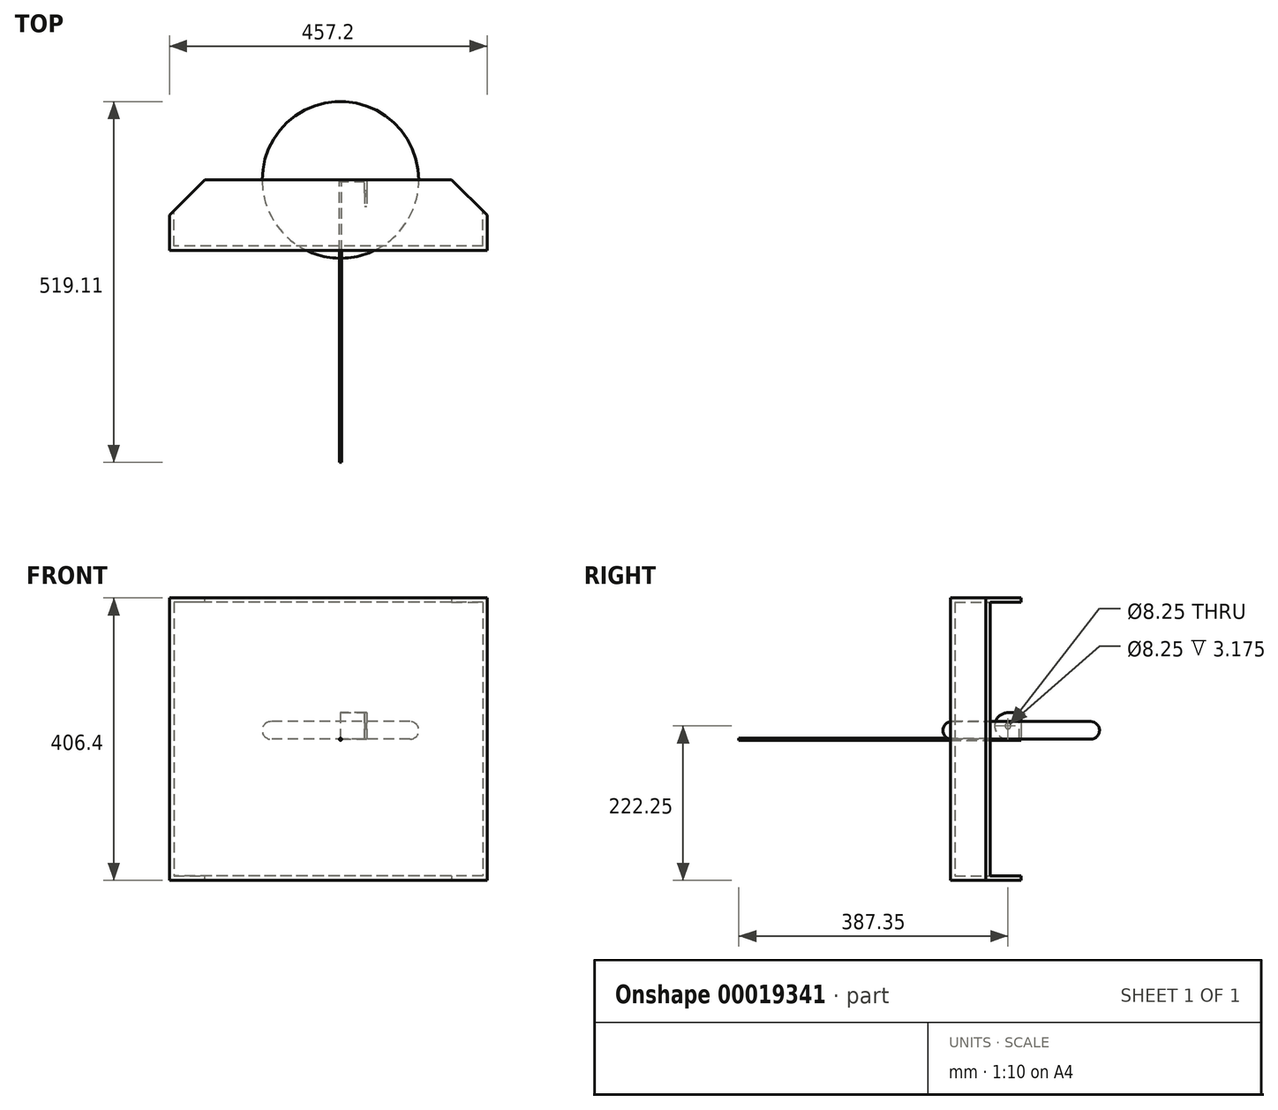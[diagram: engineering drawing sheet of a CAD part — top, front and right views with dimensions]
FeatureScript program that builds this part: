
annotation { "Feature Type Name" : "Feature", "Feature Type Description" : "" }
export const myFeature = defineFeature(function(context is Context, id is Id, definition is map)
    precondition{}
    {
        {
            var Q0;
            Q0=qCreatedBy(makeId("Top.planeOp"),FACE);
            var sketch = newSketch(context, id + "F0", { "sketchPlane" : qUnion([Q0])});
            skCircle(sketch, "E0", {"center": v(0, 0) * mm, "radius": 112.71 * mm});
            skSolve(sketch);
        }
        {
            var Q0;
            Q0=qSketchRegion(id+"F0",true);
            extrude(context, id + "F1", {"entities" : qUnion([Q0]), "depth" : 25.4 * mm});
        }
        {
            var Q0;
            Q0=qCreatedBy(makeId("Front.planeOp"),FACE);
            var sketch = newSketch(context, id + "F2", { "sketchPlane" : qUnion([Q0])});
            skCircle(sketch, "E1", {"center": v(0, 0) * mm, "radius": 1.59 * mm});
            skSolve(sketch);
        }
        {
            var Q0;
            Q0=qSketchRegion(id+"F2",true);
            extrude(context, id + "F3", {"entities" : qUnion([Q0]), "depth" : 406.4 * mm});
        }
        {
            var Q0;
            Q0=makeQuery(id+"F1.opExtrude","CAP_EDGE",EDGE,{"disambiguationData":[OSD([sQuery(id+"F0.wireOp",EDGE,"E0")])],"isStart":false});
            var Q1;
            Q1=makeQuery(id+"F1.opExtrude","CAP_EDGE",EDGE,{"disambiguationData":[OSD([sQuery(id+"F0.wireOp",EDGE,"E0")])],"isStart":true});
            fillet(context, id + "F4", {"entities" : qUnion([Q0, Q1]), "radius" : 12.7 * mm, "tangentPropagation" : true, "allowEdgeOverflow" : false});
        }
        {
            var Q0;
            Q0=qCreatedBy(makeId("Front.planeOp"),FACE);
            var sketch = newSketch(context, id + "F5", { "sketchPlane" : qUnion([Q0])});
            skLineSegment(sketch, "E2.rect.bottom", {"start": v(210.87, 203.2) * mm, "end": v(-246.33, 203.2) * mm});
            skLineSegment(sketch, "E2.rect.top", {"start": v(210.87, -203.2) * mm, "end": v(-246.33, -203.2) * mm});
            skLineSegment(sketch, "E2.rect.left", {"start": v(210.87, 203.2) * mm, "end": v(210.87, -203.2) * mm});
            skLineSegment(sketch, "E2.rect.right", {"start": v(-246.33, 203.2) * mm, "end": v(-246.33, -203.2) * mm});
            skPoint(sketch, "E2.rect.middle", {"position": v(-17.73, 0) * mm});
            skSolve(sketch);
        }
        {
            var Q0;
            Q0=qSketchRegion(id+"F5",true);
            extrude(context, id + "F6", {"entities" : qUnion([Q0]), "depth" : 101.6 * mm});
        }
        {
            var Q0;
            Q0=makeQuery(id+"F6.opExtrude","CAP_FACE",FACE,{"disambiguationData":[OSD([sQuery(id+"F5.wireOp",EDGE,"E2.rect.bottom"),sQuery(id+"F5.wireOp",EDGE,"E2.rect.top"),sQuery(id+"F5.wireOp",EDGE,"E2.rect.left"),sQuery(id+"F5.wireOp",EDGE,"E2.rect.right")])],"isStart":true});
            shell(context, id + "F7", {"entities" : qUnion([Q0]), "thickness" : 6.35 * mm});
        }
        {
            var Q0;
            Q0=makeQuery(id+"F6.opExtrude","CAP_EDGE",EDGE,{"disambiguationData":[OSD([sQuery(id+"F5.wireOp",EDGE,"E2.rect.left")])],"isStart":true});
            var Q1;
            Q1=makeQuery(id+"F6.opExtrude","CAP_EDGE",EDGE,{"disambiguationData":[OSD([sQuery(id+"F5.wireOp",EDGE,"E2.rect.right")])],"isStart":true});
            chamfer(context, id + "F8", {"entities" : qUnion([Q0, Q1]), "width" : 50.8 * mm, "tangentPropagation" : true});
        }
        {
            var Q0;
            Q0=qCreatedBy(makeId("Top.planeOp"),FACE);
            var sketch = newSketch(context, id + "F9", { "sketchPlane" : qUnion([Q0])});
            skLineSegment(sketch, "E3", {"start": v(0, 0) * mm, "end": v(38.1, 0) * mm});
            skLineSegment(sketch, "E4", {"start": v(38.1, 0) * mm, "end": v(38.1, -38.1) * mm});
            skLineSegment(sketch, "E5", {"start": v(38.1, -38.1) * mm, "end": v(34.93, -38.1) * mm});
            skLineSegment(sketch, "E6", {"start": v(34.93, -38.1) * mm, "end": v(34.93, -3.17) * mm});
            skLineSegment(sketch, "E7", {"start": v(34.92, -3.18) * mm, "end": v(0, -3.18) * mm});
            skLineSegment(sketch, "E8", {"start": v(0, -3.17) * mm, "end": v(0, 0) * mm});
            skSolve(sketch);
        }
        {
            var Q0;
            Q0=qSketchRegion(id+"F9",true);
            extrude(context, id + "F10", {"entities" : qUnion([Q0]), "depth" : 38.1 * mm});
        }
        {
            var Q0;
            Q0=makeQuery(id+"F10.opExtrude","SWEPT_FACE",FACE,{"disambiguationData":[OSD([sQuery(id+"F9.wireOp",EDGE,"E4")])]});
            var sketch = newSketch(context, id + "F11", { "sketchPlane" : qUnion([Q0])});
            skLineSegment(sketch, "E9", {"start": v(-19.05, 0) * mm, "end": v(-19.05, 38.1) * mm, "construction": true});
            skCircle(sketch, "E10", {"center": v(-19.05, 19.05) * mm, "radius": 4.12 * mm});
            skSolve(sketch);
        }
        {
            var Q0;
            Q0=makeQuery(id+"F11.imprint","IMPRINT",FACE,{"disambiguationData":[TD([[makeQuery(id+"F11.imprint","IMPRINT",EDGE,{"derivedFrom":sQuery(id+"F11.wireOp",EDGE,"E10")}),1.0]])]});
            var Q1;
            Q1=sQuery(id+"F11.wireOp",EDGE,"E10");
            extrude(context, id + "F12", {"entities" : qUnion([Q0]), "operationType" : NewBodyOperationType.REMOVE, "surfaceEntities" : qUnion([Q1]), "endBound" : BoundingType.UP_TO_NEXT, "oppositeDirection" : true, "depth" : 25.4 * mm});
        }
        {
            var Q0;
            Q0=makeQuery(id+"F10.opExtrude","CAP_EDGE",EDGE,{"disambiguationData":[OSD([sQuery(id+"F9.wireOp",EDGE,"E5")])],"isStart":true});
            var Q1;
            Q1=makeQuery(id+"F10.opExtrude","CAP_EDGE",EDGE,{"disambiguationData":[OSD([sQuery(id+"F9.wireOp",EDGE,"E5")])],"isStart":false});
            fillet(context, id + "F13", {"entities" : qUnion([Q0, Q1]), "radius" : 19.05 * mm, "tangentPropagation" : true, "allowEdgeOverflow" : false});
        }
    });
